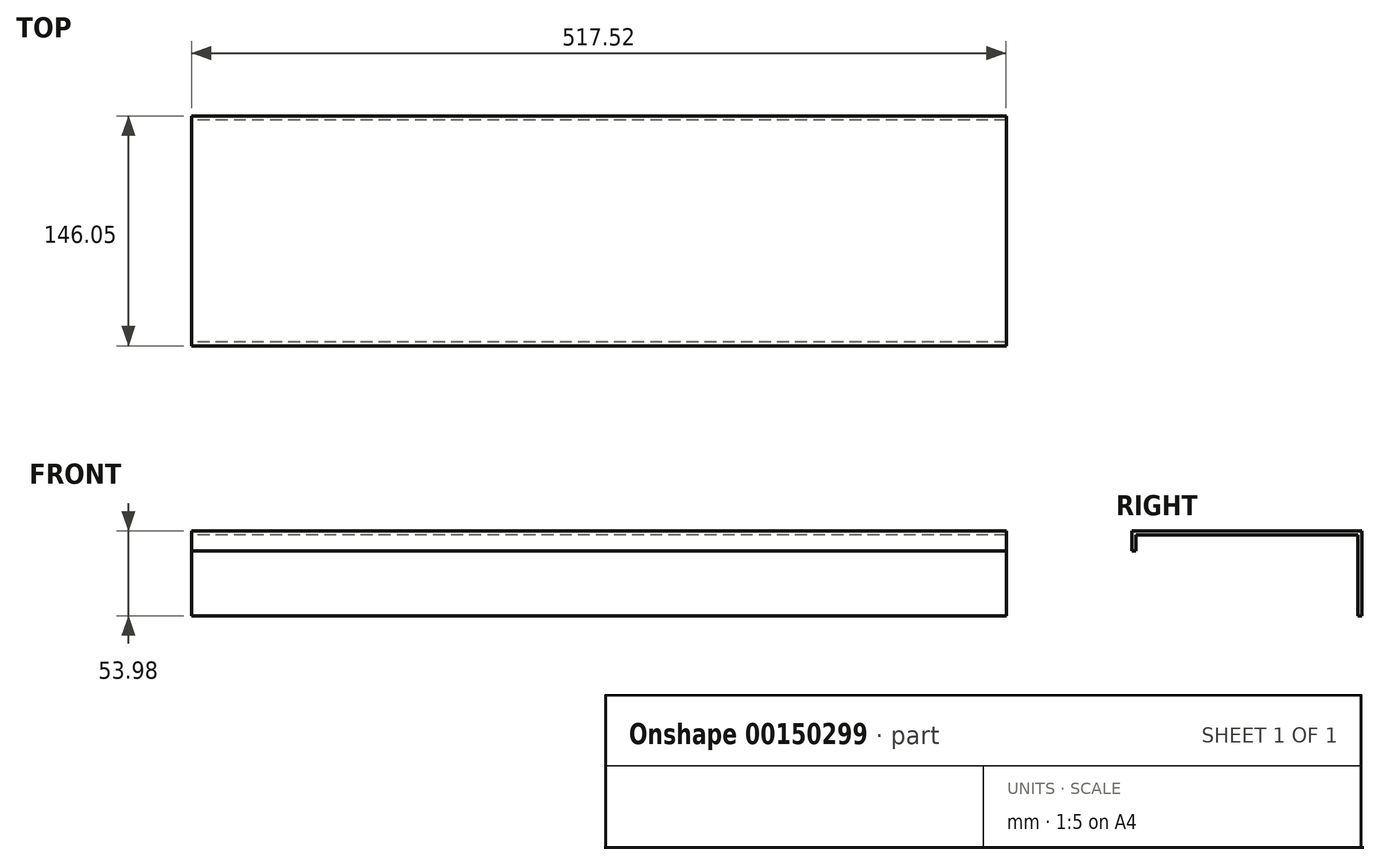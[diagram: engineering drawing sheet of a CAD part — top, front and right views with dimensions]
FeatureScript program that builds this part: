
annotation { "Feature Type Name" : "Feature", "Feature Type Description" : "" }
export const myFeature = defineFeature(function(context is Context, id is Id, definition is map)
    precondition{}
    {
        {
            var Q0;
            Q0=qCreatedBy(makeId("Right.planeOp"),FACE);
            var sketch = newSketch(context, id + "F0", { "sketchPlane" : qUnion([Q0])});
            skLineSegment(sketch, "E0", {"start": v(-85.62, 36.68) * mm, "end": v(-85.62, 49.38) * mm});
            skLineSegment(sketch, "E1", {"start": v(-85.62, 49.38) * mm, "end": v(60.43, 49.38) * mm});
            skLineSegment(sketch, "E2", {"start": v(60.43, 49.38) * mm, "end": v(60.43, -4.6) * mm});
            skLineSegment(sketch, "E3.0", {"start": v(57.89, 46.84) * mm, "end": v(57.89, -4.6) * mm});
            skLineSegment(sketch, "E3.1", {"start": v(-83.08, 46.84) * mm, "end": v(57.89, 46.84) * mm});
            skLineSegment(sketch, "E3.2", {"start": v(-83.08, 36.68) * mm, "end": v(-83.08, 46.84) * mm});
            skLineSegment(sketch, "E4", {"start": v(-85.62, 36.68) * mm, "end": v(-83.08, 36.68) * mm});
            skLineSegment(sketch, "E5", {"start": v(57.89, -4.6) * mm, "end": v(60.43, -4.6) * mm});
            skSolve(sketch);
        }
        {
            var Q0;
            Q0=makeQuery(id+"F0.imprint","IMPRINT",FACE,{"disambiguationData":[TD([[makeQuery(id+"F0.imprint","IMPRINT",EDGE,{"derivedFrom":sQuery(id+"F0.wireOp",EDGE,"E0")}),-1.0]])]});
            extrude(context, id + "F1", {"entities" : qUnion([Q0]), "depth" : 517.52 * mm});
        }
    });
